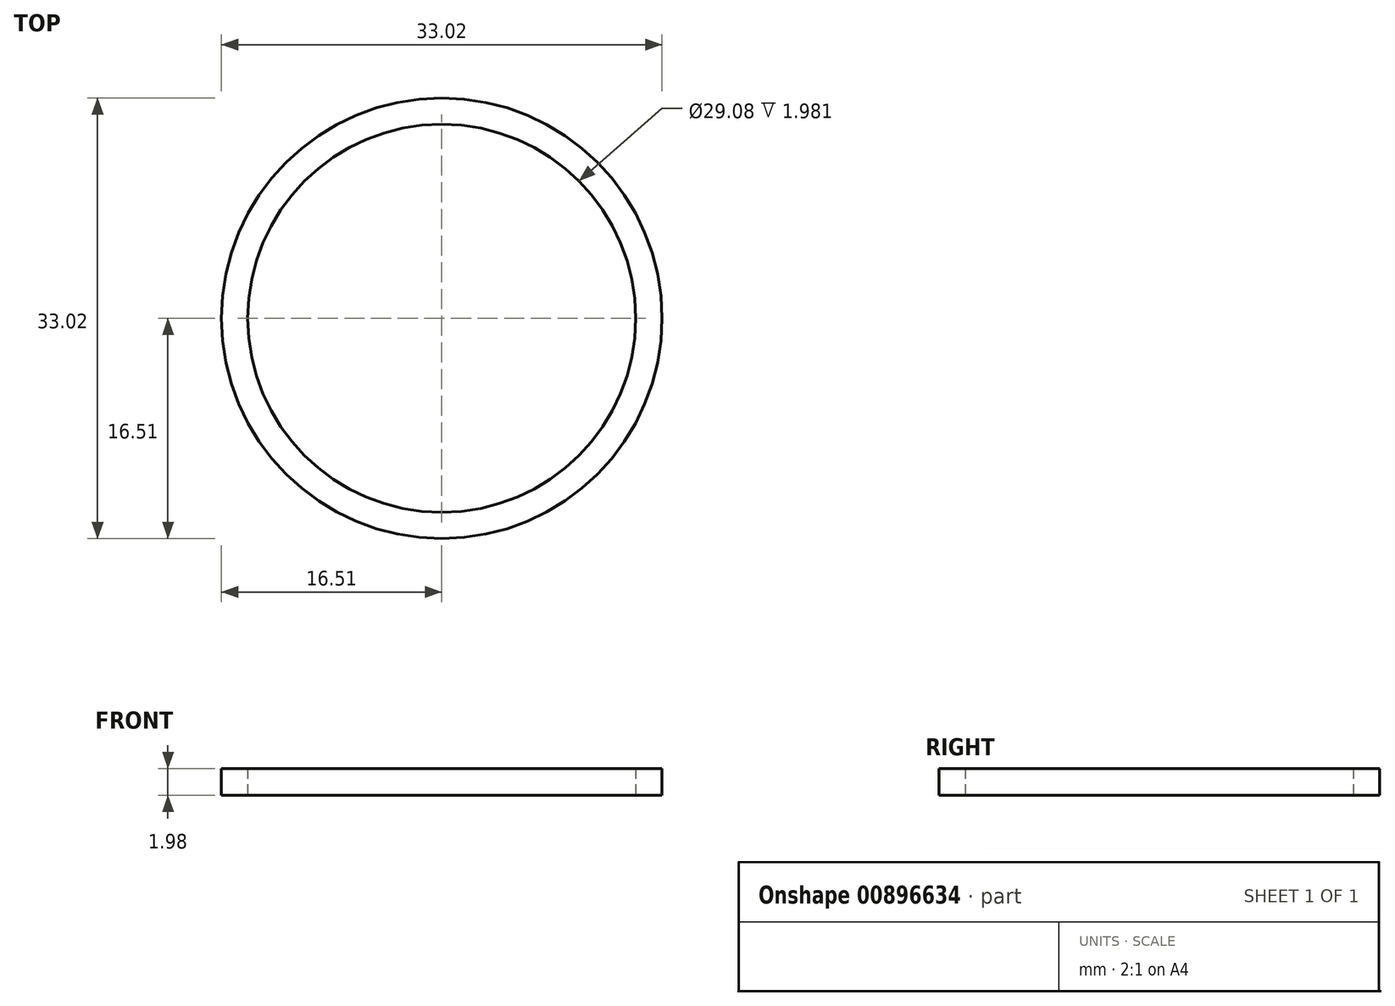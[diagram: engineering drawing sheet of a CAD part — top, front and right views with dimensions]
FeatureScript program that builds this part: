
annotation { "Feature Type Name" : "Feature", "Feature Type Description" : "" }
export const myFeature = defineFeature(function(context is Context, id is Id, definition is map)
    precondition{}
    {
        {
            var Q0;
            Q0=qCreatedBy(makeId("Top.planeOp"),FACE);
            var sketch = newSketch(context, id + "F0", { "sketchPlane" : qUnion([Q0])});
            skCircle(sketch, "E0", {"center": v(0, 0) * mm, "radius": 16.51 * mm});
            skCircle(sketch, "E1", {"center": v(0, 0) * mm, "radius": 14.54 * mm});
            skSolve(sketch);
        }
        {
            var Q0;
            Q0=makeQuery(id+"F0.imprint","IMPRINT",FACE,{"disambiguationData":[TD([[makeQuery(id+"F0.imprint","IMPRINT",EDGE,{"derivedFrom":sQuery(id+"F0.wireOp",EDGE,"E0")}),-1.0]])]});
            var Q1;
            Q1=makeQuery(id+"F0.imprint","IMPRINT",FACE,{"disambiguationData":[TD([[makeQuery(id+"F0.imprint","IMPRINT",EDGE,{"derivedFrom":sQuery(id+"F0.wireOp",EDGE,"E0")}),1.0]])]});
            extrude(context, id + "F1", {"entities" : qUnion([Q0, Q1]), "depth" : 1.98 * mm, "offsetDistance" : 25.4 * mm});
        }
    });
